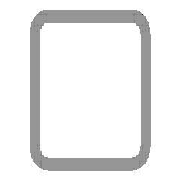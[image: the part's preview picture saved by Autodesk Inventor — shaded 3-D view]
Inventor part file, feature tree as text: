
AUTODESK INVENTOR PART (.ipt)
format: ipt  version: 2025.1 (Build 291241020, 241B)  size: 143,360 bytes
history: native  units: mm (DEFAULTED — no unit token found)
features: other x4, sketch x1, plane x1
ambient origin geometry x8: Origin, YZ Plane, XZ Plane, XY Plane, X Axis, Y Axis, Z Axis, Center Point
bodies: Solid1 (feature_tree), Body (feature_tree)
feature tree (6):
  parser-record x1  (decoder bookkeeping rows leaked as tree rows — omitted from the tree; the rows remain in map.json)
  other  "Driven Length"
  other  "Start plane"
  other  "End plane"
  sketch  "Sketch3"  dims[d3=2400.0mm d4=0.0mm d7=6.0mm d9=100.0mm d11=100.0mm d12=3.0mm d13=-0.0mm d14=2400.0mm d15=50.0mm d16=50.0mm d17=90.0deg d18=2400.0mm]
  plane  "Work Plane3"
